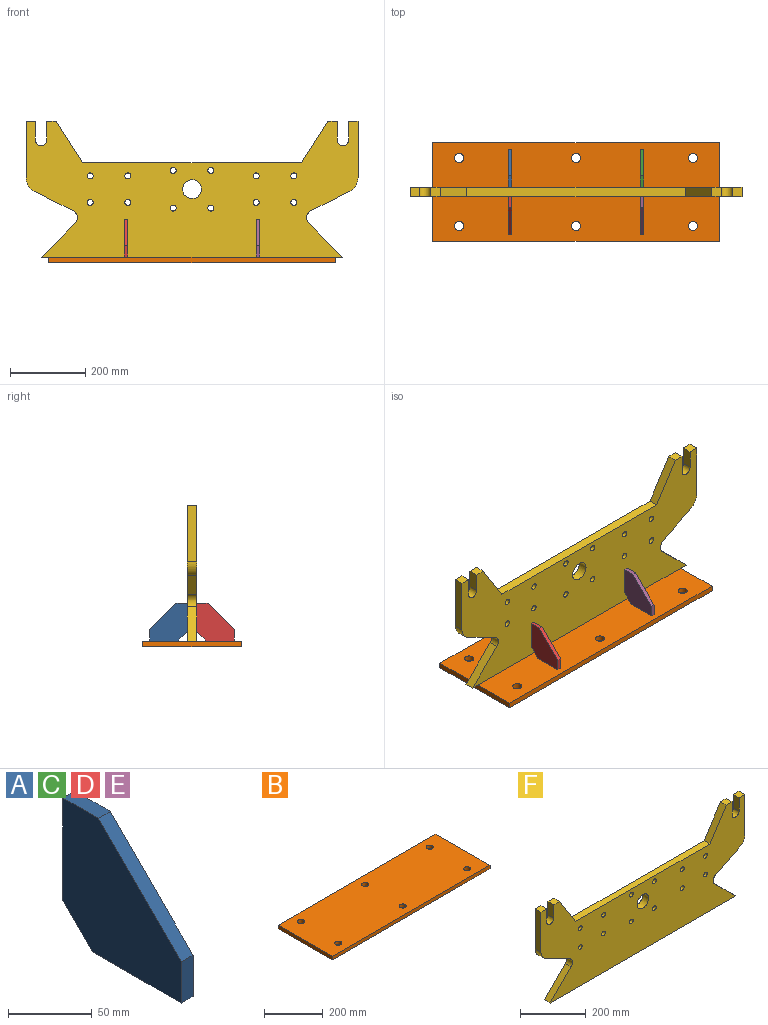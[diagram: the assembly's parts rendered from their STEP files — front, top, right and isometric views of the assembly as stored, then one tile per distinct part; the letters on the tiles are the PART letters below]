
ASSEMBLY  parts=6 mates=5
PART A: 8 faces, bbox 10x100x100 mm
  f0: plane 25x25mm, normal (0,0.71,-0.71), area 353.6mm2, adj f1,f5,f6,f7
  f1: plane 75x10mm, normal (0,1,0), area 750mm2, adj f0,f2,f6,f7
  f2: plane 30x10mm, normal (0,0,1), area 300mm2, adj f1,f3,f6,f7
  f3: plane 70x70mm, normal (0,-0.71,0.71), area 989.9mm2, adj f2,f4,f6,f7
  f4: plane 30x10mm, normal (0,-1,0), area 300mm2, adj f3,f5,f6,f7
  f5: plane 75x10mm, normal (0,0,-1), area 750mm2, adj f0,f4,f6,f7
  f6: plane 100x100mm, normal (1,0,0), area 7237.5mm2, adj f0,f1,f2,f3,f4,f5
  f7: plane 100x100mm, normal (-1,0,0), area 7237.5mm2, adj f0,f1,f2,f3,f4,f5
PART B: 12 faces, bbox 760x260x15 mm
  f0: plane 260x15mm, normal (-1,0,0), area 3900mm2, adj f1,f9,f10,f11
  f1: plane 760x15mm, normal (0,-1,0), area 11400mm2, adj f0,f2,f10,f11
  f2: plane 260x15mm, normal (1,0,0), area 3900mm2, adj f1,f9,f10,f11
  f3: cylinder r=12mm len=24mm, axis (0,0,-1), area 1131mm2, adj f10,f11
  f4: cylinder r=12mm len=24mm, axis (0,0,-1), area 1131mm2, adj f10,f11
  f5: cylinder r=12mm len=24mm, axis (0,0,-1), area 1131mm2, adj f10,f11
  f6: cylinder r=12mm len=24mm, axis (0,0,-1), area 1131mm2, adj f10,f11
  f7: cylinder r=12mm len=24mm, axis (0,0,-1), area 1131mm2, adj f10,f11
  f8: cylinder r=12mm len=24mm, axis (0,0,-1), area 1131mm2, adj f10,f11
  f9: plane 760x15mm, normal (0,1,0), area 11400mm2, adj f0,f2,f10,f11
  f10: plane 760x260mm, normal (0,0,1), area 194885.7mm2, adj f0,f1,f2,f3,f4,f5,f6,f7
  f11: plane 760x260mm, normal (0,0,-1), area 194885.7mm2, adj f0,f1,f2,f3,f4,f5,f6,f7
PART C: same geometry as A
PART D: same geometry as A
PART E: same geometry as A
PART F: 39 faces, bbox 880x25x360 mm
  f0: plane 580x25mm, normal (0,0,1), area 14500mm2, adj f1,f34,f35,f36
  f1: plane 110x70mm, normal (0.84,0,0.54), area 3259.6mm2, adj f0,f2,f35,f36
  f2: plane 25x25mm, normal (0,0,1), area 625mm2, adj f1,f3,f35,f36
  f3: plane 50x25mm, normal (-1,0,0), area 1250mm2, adj f2,f4,f35,f36
  f4: cylinder r=15mm len=30mm, axis (0,1,0), area 1178.1mm2, adj f3,f5,f35,f36
  f5: plane 50x25mm, normal (1,0,0), area 1250mm2, adj f4,f6,f35,f36
  f6: plane 25x25mm, normal (0,0,1), area 625mm2, adj f5,f7,f35,f36
  f7: plane 150x25mm, normal (-1,0,0), area 3750mm2, adj f6,f8,f35,f36
  f8: cylinder r=40mm len=35.75mm, axis (0,1,0), area 1105.4mm2, adj f7,f9,f35,f36
  f9: plane 103.2x51.82mm, normal (-0.45,0,-0.89), area 2887mm2, adj f8,f35,f36,f37
  f10: plane 90.42x90.42mm, normal (-0.71,0,0.71), area 3196.6mm2, adj f11,f35,f36,f37
  f11: plane 800x25mm, normal (0,0,-1), area 20000mm2, adj f10,f12,f35,f36
  f12: plane 90.42x90.42mm, normal (0.71,0,0.71), area 3196.6mm2, adj f11,f35,f36,f38
  f13: plane 103.2x51.82mm, normal (0.45,0,-0.89), area 2887mm2, adj f14,f35,f36,f38
  f14: cylinder r=40mm len=35.75mm, axis (0,1,0), area 1105.4mm2, adj f13,f15,f35,f36
  f15: plane 150x25mm, normal (1,0,0), area 3750mm2, adj f14,f16,f35,f36
  f16: plane 25x25mm, normal (0,0,1), area 625mm2, adj f15,f17,f35,f36
  f17: plane 50x25mm, normal (-1,0,0), area 1250mm2, adj f16,f18,f35,f36
  f18: cylinder r=15mm len=30mm, axis (0,1,0), area 1178.1mm2, adj f17,f19,f35,f36
  f19: plane 50x25mm, normal (1,0,0), area 1250mm2, adj f18,f20,f35,f36
  f20: plane 25x25mm, normal (0,0,1), area 625mm2, adj f19,f34,f35,f36
  f21: cylinder r=8mm len=25mm, axis (0,1,0), area 1256.6mm2, adj f35,f36
  f22: cylinder r=8mm len=25mm, axis (0,1,0), area 1256.6mm2, adj f35,f36
  f23: cylinder r=8mm len=25mm, axis (0,1,0), area 1256.6mm2, adj f35,f36
  f24: cylinder r=8mm len=25mm, axis (0,1,0), area 1256.6mm2, adj f35,f36
  f25: cylinder r=8mm len=25mm, axis (0,1,0), area 1256.6mm2, adj f35,f36
  f26: cylinder r=8mm len=25mm, axis (0,1,0), area 1256.6mm2, adj f35,f36
  f27: cylinder r=8mm len=25mm, axis (0,1,0), area 1256.6mm2, adj f35,f36
  f28: cylinder r=8mm len=25mm, axis (0,1,0), area 1256.6mm2, adj f35,f36
  f29: cylinder r=25mm len=50mm, axis (0,1,0), area 3927mm2, adj f35,f36
  f30: cylinder r=8mm len=25mm, axis (0,1,0), area 1256.6mm2, adj f35,f36
  f31: cylinder r=8mm len=25mm, axis (0,1,0), area 1256.6mm2, adj f35,f36
  f32: cylinder r=8mm len=25mm, axis (0,1,0), area 1256.6mm2, adj f35,f36
  f33: cylinder r=8mm len=25mm, axis (0,1,0), area 1256.6mm2, adj f35,f36
  f34: plane 110x70mm, normal (-0.84,0,0.54), area 3259.6mm2, adj f0,f20,f35,f36
  f35: plane 880x360mm, normal (0,-1,0), area 205164.3mm2, adj f0,f1,f2,f3,f4,f5,f6,f7
  f36: plane 880x360mm, normal (0,1,0), area 205164.3mm2, adj f0,f1,f2,f3,f4,f5,f6,f7
  f37: cylinder r=20mm len=32.02mm, axis (0,-1,0), area 945.4mm2, adj f9,f10,f35,f36
  f38: cylinder r=20mm len=32.02mm, axis (0,1,0), area 945.4mm2, adj f12,f13,f35,f36
PLACE A rot(axis=(0,0,1),180deg) t=(-221.57,81.42,-1.97)mm
PLACE B t=(-51.57,18.92,-66.97)mm fixed
PLACE C rot(axis=(0,0,1),180deg) t=(128.43,81.42,-1.97)mm
PLACE D t=(-231.57,-43.58,-1.97)mm
PLACE E t=(118.43,-43.58,-1.97)mm
PLACE F t=(-51.57,31.42,58.03)mm
MATE fastened B.f10 <-> F.f11  axis (0,0,1) through (-51.57,18.92,-51.97)mm
MATE fastened E.f1 <-> F.f35  axis (0,1,0) through (123.43,6.42,10.53)mm
MATE fastened D.f1 <-> F.f35  axis (0,1,0) through (-226.57,6.42,10.53)mm
MATE fastened F.f36 <-> C.f1  axis (0,1,0) through (123.43,31.42,10.53)mm
MATE fastened F.f36 <-> A.f1  axis (0,1,0) through (-226.57,31.42,10.53)mm
